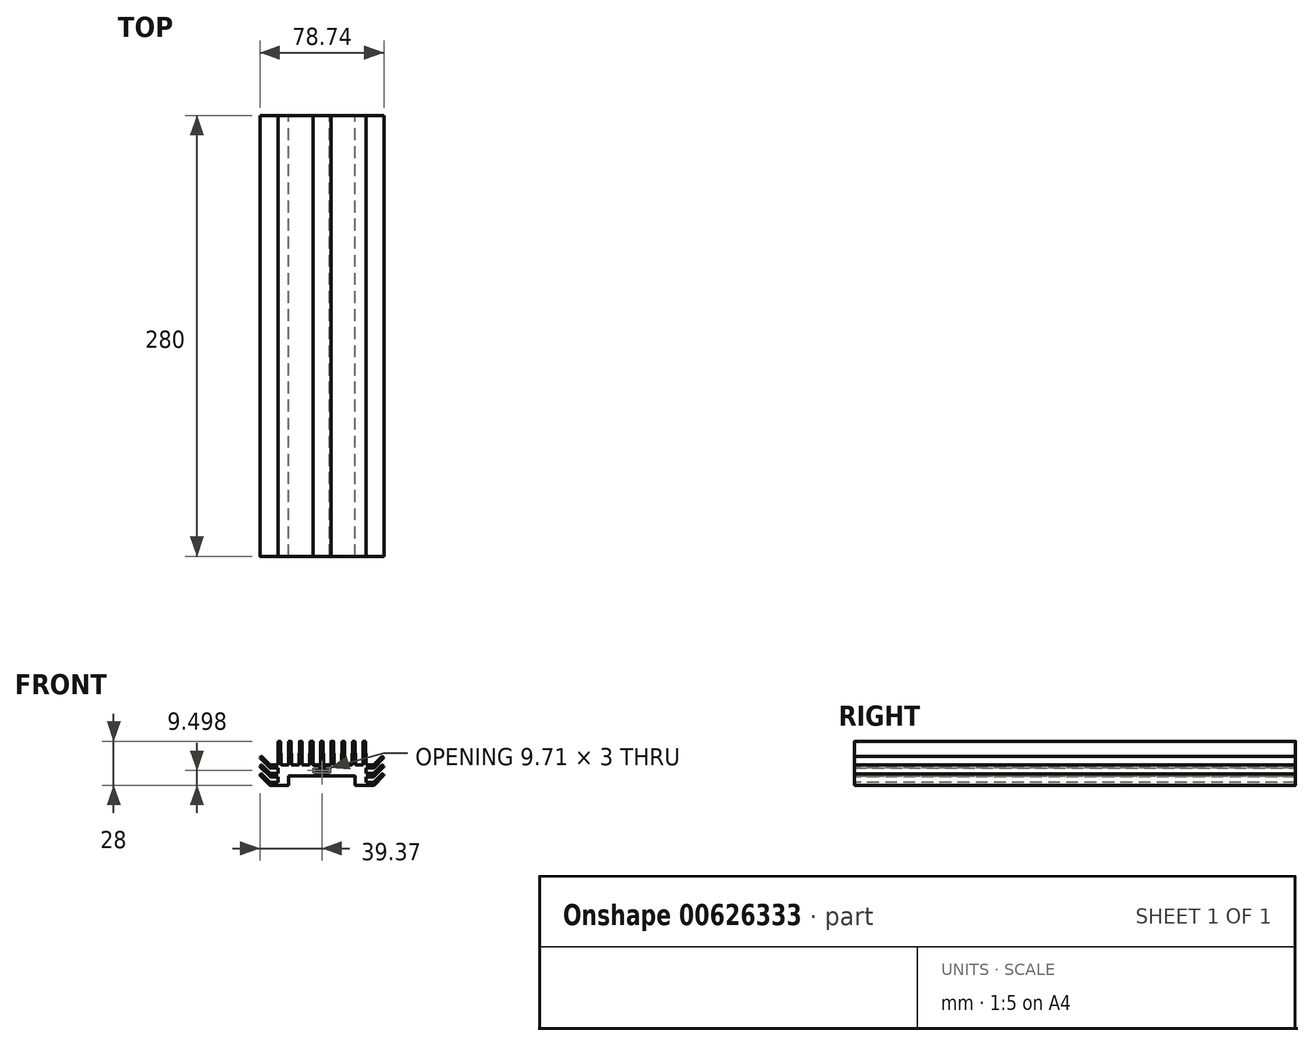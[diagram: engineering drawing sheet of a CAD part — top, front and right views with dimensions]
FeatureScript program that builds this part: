
annotation { "Feature Type Name" : "Feature", "Feature Type Description" : "" }
export const myFeature = defineFeature(function(context is Context, id is Id, definition is map)
    precondition{}
    {
        {
            var Q0;
            Q0=qCreatedBy(makeId("Front.planeOp"),FACE);
            var sketch = newSketch(context, id + "F0", { "sketchPlane" : qUnion([Q0])});
            skLineSegment(sketch, "E0.2.0.0", {"start": v(-26.25, 18.3) * mm, "end": v(-26, 3.7) * mm});
            skLineSegment(sketch, "E0.2.0.1", {"start": v(-25.8, 3.5) * mm, "end": v(-21.45, 3.5) * mm});
            skLineSegment(sketch, "E0.2.0.2", {"start": v(-28, 3.7) * mm, "end": v(-27.75, 18.3) * mm});
            skLineSegment(sketch, "E0.2.0.3", {"start": v(-27.55, 18.5) * mm, "end": v(-26.45, 18.5) * mm});
            skLineSegment(sketch, "E0.3.0.0", {"start": v(-19.5, 18.3) * mm, "end": v(-19.25, 3.7) * mm});
            skLineSegment(sketch, "E0.3.0.1", {"start": v(-19.05, 3.5) * mm, "end": v(-14.7, 3.5) * mm});
            skLineSegment(sketch, "E0.3.0.2", {"start": v(-21.25, 3.7) * mm, "end": v(-21, 18.3) * mm});
            skLineSegment(sketch, "E0.3.0.3", {"start": v(-20.8, 18.5) * mm, "end": v(-19.7, 18.5) * mm});
            skLineSegment(sketch, "E0.4.0.0", {"start": v(-12.75, 18.3) * mm, "end": v(-12.5, 3.7) * mm});
            skLineSegment(sketch, "E0.4.0.1", {"start": v(-12.3, 3.5) * mm, "end": v(-7.95, 3.5) * mm});
            skLineSegment(sketch, "E0.4.0.2", {"start": v(-14.5, 3.7) * mm, "end": v(-14.25, 18.3) * mm});
            skLineSegment(sketch, "E0.4.0.3", {"start": v(-14.05, 18.5) * mm, "end": v(-12.95, 18.5) * mm});
            skLineSegment(sketch, "E0.5.0.0", {"start": v(-5.75, 18.3) * mm, "end": v(-5.75, 3.7) * mm});
            skLineSegment(sketch, "E0.5.0.1", {"start": v(-5.55, 3.5) * mm, "end": v(-1.2, 3.5) * mm});
            skLineSegment(sketch, "E0.5.0.2", {"start": v(-7.75, 3.7) * mm, "end": v(-7.5, 18.3) * mm});
            skLineSegment(sketch, "E0.5.0.3", {"start": v(-7.3, 18.5) * mm, "end": v(-5.95, 18.5) * mm});
            skLineSegment(sketch, "E1.6.6.0", {"start": v(-1, 3.7) * mm, "end": v(-0.75, 18.3) * mm});
            skLineSegment(sketch, "E1.9.6.0", {"start": v(-0.55, 18.5) * mm, "end": v(0, 18.5) * mm});
            skPoint(sketch, "E2", {"position": v(0, 18.5) * mm});
            skLineSegment(sketch, "E3", {"start": v(0, 18.5) * mm, "end": v(0, 1.5) * mm});
            skLineSegment(sketch, "E4", {"start": v(-4.85, 1.3) * mm, "end": v(-4.85, -1.3) * mm});
            skLineSegment(sketch, "E5", {"start": v(0, -1.5) * mm, "end": v(0, -3.5) * mm});
            skPoint(sketch, "E6.visualSharp", {"position": v(-27.75, 18.5) * mm});
            skArc(sketch, "E6.filletArc", {"start": v(-27.55, 18.5) * mm, "mid": v(-27.7, 18.44) * mm, "end": v(-27.75, 18.3) * mm});
            skPoint(sketch, "E7.visualSharp", {"position": v(-26.25, 18.5) * mm});
            skArc(sketch, "E7.filletArc", {"start": v(-26.25, 18.3) * mm, "mid": v(-26.3, 18.44) * mm, "end": v(-26.45, 18.5) * mm});
            skPoint(sketch, "E8.visualSharp", {"position": v(-21, 18.5) * mm});
            skArc(sketch, "E8.filletArc", {"start": v(-20.8, 18.5) * mm, "mid": v(-20.94, 18.44) * mm, "end": v(-21, 18.3) * mm});
            skPoint(sketch, "E9.visualSharp", {"position": v(-19.5, 18.5) * mm});
            skArc(sketch, "E9.filletArc", {"start": v(-19.5, 18.3) * mm, "mid": v(-19.56, 18.44) * mm, "end": v(-19.7, 18.5) * mm});
            skPoint(sketch, "E10.visualSharp", {"position": v(-14.25, 18.5) * mm});
            skArc(sketch, "E10.filletArc", {"start": v(-14.05, 18.5) * mm, "mid": v(-14.2, 18.44) * mm, "end": v(-14.25, 18.3) * mm});
            skPoint(sketch, "E11.visualSharp", {"position": v(-12.75, 18.5) * mm});
            skArc(sketch, "E11.filletArc", {"start": v(-12.75, 18.3) * mm, "mid": v(-12.8, 18.44) * mm, "end": v(-12.95, 18.5) * mm});
            skPoint(sketch, "E12.visualSharp", {"position": v(-7.5, 18.5) * mm});
            skArc(sketch, "E12.filletArc", {"start": v(-7.3, 18.5) * mm, "mid": v(-7.44, 18.44) * mm, "end": v(-7.5, 18.3) * mm});
            skPoint(sketch, "E13.visualSharp", {"position": v(-5.75, 18.5) * mm});
            skArc(sketch, "E13.filletArc", {"start": v(-5.75, 18.3) * mm, "mid": v(-5.8, 18.44) * mm, "end": v(-5.95, 18.5) * mm});
            skPoint(sketch, "E14.visualSharp", {"position": v(-0.75, 18.5) * mm});
            skArc(sketch, "E14.filletArc", {"start": v(-0.55, 18.5) * mm, "mid": v(-0.7, 18.44) * mm, "end": v(-0.75, 18.3) * mm});
            skPoint(sketch, "E15.visualSharp", {"position": v(0, 1.5) * mm});
            skPoint(sketch, "E16.visualSharp", {"position": v(-4.85, 1.5) * mm});
            skArc(sketch, "E16.filletArc", {"start": v(-4.65, 1.5) * mm, "mid": v(-4.8, 1.44) * mm, "end": v(-4.85, 1.3) * mm});
            skPoint(sketch, "E17.visualSharp", {"position": v(-4.85, -1.5) * mm});
            skArc(sketch, "E17.filletArc", {"start": v(-4.85, -1.3) * mm, "mid": v(-4.8, -1.44) * mm, "end": v(-4.65, -1.5) * mm});
            skPoint(sketch, "E18.visualSharp", {"position": v(0, -1.5) * mm});
            skPoint(sketch, "E19.visualSharp", {"position": v(0, -3.5) * mm});
            skPoint(sketch, "E20.visualSharp", {"position": v(-26, 3.5) * mm});
            skArc(sketch, "E20.filletArc", {"start": v(-26, 3.7) * mm, "mid": v(-25.94, 3.56) * mm, "end": v(-25.8, 3.5) * mm});
            skPoint(sketch, "E21.visualSharp", {"position": v(-21.25, 3.5) * mm});
            skArc(sketch, "E21.filletArc", {"start": v(-21.45, 3.5) * mm, "mid": v(-21.3, 3.56) * mm, "end": v(-21.25, 3.7) * mm});
            skPoint(sketch, "E22.visualSharp", {"position": v(-19.25, 3.5) * mm});
            skArc(sketch, "E22.filletArc", {"start": v(-19.25, 3.7) * mm, "mid": v(-19.2, 3.56) * mm, "end": v(-19.05, 3.5) * mm});
            skPoint(sketch, "E23.visualSharp", {"position": v(-14.5, 3.5) * mm});
            skArc(sketch, "E23.filletArc", {"start": v(-14.7, 3.5) * mm, "mid": v(-14.56, 3.56) * mm, "end": v(-14.5, 3.7) * mm});
            skPoint(sketch, "E24.visualSharp", {"position": v(-12.5, 3.5) * mm});
            skArc(sketch, "E24.filletArc", {"start": v(-12.5, 3.7) * mm, "mid": v(-12.44, 3.56) * mm, "end": v(-12.3, 3.5) * mm});
            skPoint(sketch, "E25.visualSharp", {"position": v(-7.75, 3.5) * mm});
            skArc(sketch, "E25.filletArc", {"start": v(-7.95, 3.5) * mm, "mid": v(-7.8, 3.56) * mm, "end": v(-7.75, 3.7) * mm});
            skPoint(sketch, "E26.visualSharp", {"position": v(-5.75, 3.5) * mm});
            skArc(sketch, "E26.filletArc", {"start": v(-5.75, 3.7) * mm, "mid": v(-5.7, 3.56) * mm, "end": v(-5.55, 3.5) * mm});
            skPoint(sketch, "E27.visualSharp", {"position": v(-1, 3.5) * mm});
            skArc(sketch, "E27.filletArc", {"start": v(-1.2, 3.5) * mm, "mid": v(-1.06, 3.56) * mm, "end": v(-1, 3.7) * mm});
            skLineSegment(sketch, "E28", {"start": v(-4.65, 1.5) * mm, "end": v(0, 1.5) * mm});
            skLineSegment(sketch, "E29", {"start": v(-4.65, -1.5) * mm, "end": v(0, -1.5) * mm});
            skLineSegment(sketch, "E30", {"start": v(-21.15, -3.7) * mm, "end": v(-21.15, -9.3) * mm});
            skPoint(sketch, "E31.visualSharp", {"position": v(-21.15, -9.5) * mm});
            skArc(sketch, "E31.filletArc", {"start": v(-21.35, -9.5) * mm, "mid": v(-21.2, -9.44) * mm, "end": v(-21.15, -9.3) * mm});
            skPoint(sketch, "E32.visualSharp", {"position": v(-21.15, -3.5) * mm});
            skArc(sketch, "E32.filletArc", {"start": v(-20.95, -3.5) * mm, "mid": v(-21.1, -3.56) * mm, "end": v(-21.15, -3.7) * mm});
            skLineSegment(sketch, "E33", {"start": v(-28, 3.7) * mm, "end": v(-28, -9.5) * mm});
            skLineSegment(sketch, "E34", {"start": v(-21.35, -9.5) * mm, "end": v(-28, -9.5) * mm});
            skLineSegment(sketch, "E35", {"start": v(-20.95, -3.5) * mm, "end": v(0, -3.5) * mm});
            skSolve(sketch);
        }
        {
            var Q0;
            Q0=qSketchRegion(id+"F0",true);
            extrude(context, id + "F1", {"entities" : qUnion([Q0]), "depth" : 280 * mm, "offsetDistance" : 25 * mm});
        }
        {
            var Q0;
            Q0=makeQuery(id+"F1.opExtrude","CAP_FACE",FACE,{"disambiguationData":[OSD([sQuery(id+"F0.wireOp",EDGE,"bL3qZI64-7qrA-8tBo-xELN-WwCQw7n5xeQu"),sQuery(id+"F0.wireOp",EDGE,"nefEkcPL-9hmu-xnLm-Q7lG-tzpoaju1hbQN"),sQuery(id+"F0.wireOp",EDGE,"E0.1.0.0"),sQuery(id+"F0.wireOp",EDGE,"E0.1.0.1"),sQuery(id+"F0.wireOp",EDGE,"E0.1.0.2"),sQuery(id+"F0.wireOp",EDGE,"E0.1.0.3"),sQuery(id+"F0.wireOp",EDGE,"E0.2.0.0"),sQuery(id+"F0.wireOp",EDGE,"E0.2.0.1"),sQuery(id+"F0.wireOp",EDGE,"E0.2.0.2"),sQuery(id+"F0.wireOp",EDGE,"E0.2.0.3"),sQuery(id+"F0.wireOp",EDGE,"E0.3.0.0"),sQuery(id+"F0.wireOp",EDGE,"E0.3.0.1"),sQuery(id+"F0.wireOp",EDGE,"E0.3.0.2"),sQuery(id+"F0.wireOp",EDGE,"E0.3.0.3"),sQuery(id+"F0.wireOp",EDGE,"E0.4.0.0"),sQuery(id+"F0.wireOp",EDGE,"E0.4.0.1"),sQuery(id+"F0.wireOp",EDGE,"E0.4.0.2"),sQuery(id+"F0.wireOp",EDGE,"E0.4.0.3"),sQuery(id+"F0.wireOp",EDGE,"E0.5.0.0"),sQuery(id+"F0.wireOp",EDGE,"E0.5.0.1"),sQuery(id+"F0.wireOp",EDGE,"E0.5.0.2"),sQuery(id+"F0.wireOp",EDGE,"E0.5.0.3"),sQuery(id+"F0.wireOp",EDGE,"E1.6.6.0"),sQuery(id+"F0.wireOp",EDGE,"E1.9.6.0"),sQuery(id+"F0.wireOp",EDGE,"E3"),sQuery(id+"F0.wireOp",EDGE,"E4"),sQuery(id+"F0.wireOp",EDGE,"E5"),sQuery(id+"F0.wireOp",EDGE,"mlO0Lyb2-eVYo-AatF-SlvP-83DAQH0pbuAu"),sQuery(id+"F0.wireOp",EDGE,"1c295024-f0d5-4380-9586-7d7894610ec9.filletArc"),sQuery(id+"F0.wireOp",EDGE,"2c5bb03b-c66e-477a-8ee8-765ec2279287.filletArc"),sQuery(id+"F0.wireOp",EDGE,"E6.filletArc"),sQuery(id+"F0.wireOp",EDGE,"E7.filletArc"),sQuery(id+"F0.wireOp",EDGE,"E8.filletArc"),sQuery(id+"F0.wireOp",EDGE,"E9.filletArc"),sQuery(id+"F0.wireOp",EDGE,"E10.filletArc"),sQuery(id+"F0.wireOp",EDGE,"E11.filletArc"),sQuery(id+"F0.wireOp",EDGE,"E12.filletArc"),sQuery(id+"F0.wireOp",EDGE,"E13.filletArc"),sQuery(id+"F0.wireOp",EDGE,"E14.filletArc"),sQuery(id+"F0.wireOp",EDGE,"E16.filletArc"),sQuery(id+"F0.wireOp",EDGE,"E17.filletArc"),sQuery(id+"F0.wireOp",EDGE,"3fa5c7a0-46de-4f7c-b7f0-d3e079dab4d4.filletArc"),sQuery(id+"F0.wireOp",EDGE,"1a05ea91-b8e8-4e60-8976-cabcb86d6e5d.filletArc"),sQuery(id+"F0.wireOp",EDGE,"4ed3edbc-86c1-4c2d-b3db-7962da8c7f3b.filletArc"),sQuery(id+"F0.wireOp",EDGE,"df53fec7-61cd-4923-a6ae-b9e3b851a0f2.filletArc"),sQuery(id+"F0.wireOp",EDGE,"27feb3de-e673-4ea3-928d-deec6766394d.filletArc"),sQuery(id+"F0.wireOp",EDGE,"473c6a5f-9318-4648-8a10-d55a2b371333.filletArc"),sQuery(id+"F0.wireOp",EDGE,"E20.filletArc"),sQuery(id+"F0.wireOp",EDGE,"E21.filletArc"),sQuery(id+"F0.wireOp",EDGE,"E22.filletArc"),sQuery(id+"F0.wireOp",EDGE,"E23.filletArc"),sQuery(id+"F0.wireOp",EDGE,"E24.filletArc"),sQuery(id+"F0.wireOp",EDGE,"E25.filletArc"),sQuery(id+"F0.wireOp",EDGE,"E26.filletArc"),sQuery(id+"F0.wireOp",EDGE,"E27.filletArc"),sQuery(id+"F0.wireOp",EDGE,"E28"),sQuery(id+"F0.wireOp",EDGE,"E29"),sQuery(id+"F0.wireOp",EDGE,"uo7RkyCL-c98j-zEhM-1sWP-hJWaIm8JIuHS"),sQuery(id+"F0.wireOp",EDGE,"UyrvhKvo-Hriy-DGAL-Pid4-MuuIVOQ2I04g"),sQuery(id+"F0.wireOp",EDGE,"U6ICKPt3-iNcd-rmJ2-pTeO-fHKRQgZmkzro"),sQuery(id+"F0.wireOp",EDGE,"cJHcNlIk-0kYQ-5AfO-mOoR-XwhJbZEzOTLT"),sQuery(id+"F0.wireOp",EDGE,"E30"),sQuery(id+"F0.wireOp",EDGE,"E31.filletArc"),sQuery(id+"F0.wireOp",EDGE,"1ba531c4-4689-4158-b5fc-088271326b5e.filletArc"),sQuery(id+"F0.wireOp",EDGE,"E32.filletArc")])],"isStart":false});
            var sketch = newSketch(context, id + "F2", { "sketchPlane" : qUnion([Q0])});
            skLineSegment(sketch, "E36", {"start": v(-28, -7.5) * mm, "end": v(-32.79, -7.5) * mm});
            skLineSegment(sketch, "E37", {"start": v(-28, -9.5) * mm, "end": v(-33, -9.5) * mm});
            skLineSegment(sketch, "E38", {"start": v(-32.93, -7.45) * mm, "end": v(-38.25, -2.13) * mm});
            skLineSegment(sketch, "E39", {"start": v(-33.06, -9.44) * mm, "end": v(-39.3, -3.19) * mm});
            skLineSegment(sketch, "E40", {"start": v(-38.53, -2.13) * mm, "end": v(-39.3, -2.9) * mm});
            skLineSegment(sketch, "E41", {"start": v(-28, -7.5) * mm, "end": v(-28, -9.5) * mm});
            skLineSegment(sketch, "E42.direction2", {"start": v(-33, -9.5) * mm, "end": v(-33, -4) * mm, "construction": true});
            skPoint(sketch, "E43.visualSharp", {"position": v(-32.87, -7.5) * mm});
            skArc(sketch, "E43.filletArc", {"start": v(-32.93, -7.45) * mm, "mid": v(-32.87, -7.49) * mm, "end": v(-32.79, -7.5) * mm});
            skPoint(sketch, "E44.visualSharp", {"position": v(-38.39, -1.99) * mm});
            skArc(sketch, "E44.filletArc", {"start": v(-38.25, -2.13) * mm, "mid": v(-38.39, -2.07) * mm, "end": v(-38.53, -2.13) * mm});
            skPoint(sketch, "E45.visualSharp", {"position": v(-39.45, -3.05) * mm});
            skArc(sketch, "E45.filletArc", {"start": v(-39.3, -2.9) * mm, "mid": v(-39.37, -3.05) * mm, "end": v(-39.3, -3.19) * mm});
            skPoint(sketch, "E46.visualSharp", {"position": v(-33, -9.5) * mm});
            skArc(sketch, "E46.filletArc", {"start": v(-33.06, -9.44) * mm, "mid": v(-33, -9.48) * mm, "end": v(-32.91, -9.5) * mm});
            skLineSegment(sketch, "E47.0.1.0", {"start": v(-32.93, -1.95) * mm, "end": v(-38.25, 3.37) * mm});
            skLineSegment(sketch, "E47.0.1.1", {"start": v(-33.06, -3.94) * mm, "end": v(-39.3, 2.31) * mm});
            skPoint(sketch, "E47.0.1.2", {"position": v(-38.39, 3.51) * mm});
            skLineSegment(sketch, "E47.0.1.3", {"start": v(-28, -4) * mm, "end": v(-33, -4) * mm});
            skLineSegment(sketch, "E47.0.1.4", {"start": v(-28, -2) * mm, "end": v(-28, -4) * mm});
            skPoint(sketch, "E47.0.1.5", {"position": v(-33, -4) * mm});
            skLineSegment(sketch, "E47.0.1.6", {"start": v(-28, -2) * mm, "end": v(-32.79, -2) * mm});
            skPoint(sketch, "E47.0.1.7", {"position": v(-39.45, 2.45) * mm});
            skPoint(sketch, "E47.0.1.8", {"position": v(-32.87, -2) * mm});
            skLineSegment(sketch, "E47.0.1.9", {"start": v(-33, -4) * mm, "end": v(-33, 1.5) * mm, "construction": true});
            skLineSegment(sketch, "E47.0.1.10", {"start": v(-33, -4) * mm, "end": v(-33, 1.5) * mm, "construction": true});
            skLineSegment(sketch, "E47.0.1.11", {"start": v(-38.53, 3.37) * mm, "end": v(-39.3, 2.6) * mm});
            skArc(sketch, "E47.0.1.12", {"start": v(-38.25, 3.37) * mm, "mid": v(-38.39, 3.43) * mm, "end": v(-38.53, 3.37) * mm});
            skArc(sketch, "E47.0.1.13", {"start": v(-39.3, 2.6) * mm, "mid": v(-39.37, 2.45) * mm, "end": v(-39.3, 2.31) * mm});
            skArc(sketch, "E47.0.1.14", {"start": v(-32.93, -1.95) * mm, "mid": v(-32.87, -1.99) * mm, "end": v(-32.79, -2) * mm});
            skArc(sketch, "E47.0.1.15", {"start": v(-33.06, -3.94) * mm, "mid": v(-33, -3.98) * mm, "end": v(-32.91, -4) * mm});
            skLineSegment(sketch, "E47.0.2.0", {"start": v(-32.93, 3.55) * mm, "end": v(-38.25, 8.87) * mm});
            skLineSegment(sketch, "E47.0.2.1", {"start": v(-33.06, 1.56) * mm, "end": v(-39.3, 7.81) * mm});
            skPoint(sketch, "E47.0.2.2", {"position": v(-38.39, 9.01) * mm});
            skLineSegment(sketch, "E47.0.2.3", {"start": v(-28, 1.5) * mm, "end": v(-33, 1.5) * mm});
            skLineSegment(sketch, "E47.0.2.4", {"start": v(-28, 3.5) * mm, "end": v(-28, 1.5) * mm});
            skPoint(sketch, "E47.0.2.5", {"position": v(-33, 1.5) * mm});
            skLineSegment(sketch, "E47.0.2.6", {"start": v(-28, 3.5) * mm, "end": v(-32.79, 3.5) * mm});
            skPoint(sketch, "E47.0.2.7", {"position": v(-39.45, 7.95) * mm});
            skPoint(sketch, "E47.0.2.8", {"position": v(-32.87, 3.5) * mm});
            skLineSegment(sketch, "E47.0.2.9", {"start": v(-33, 1.5) * mm, "end": v(-33, 7) * mm, "construction": true});
            skLineSegment(sketch, "E47.0.2.10", {"start": v(-33, 1.5) * mm, "end": v(-33, 7) * mm, "construction": true});
            skLineSegment(sketch, "E47.0.2.11", {"start": v(-38.53, 8.87) * mm, "end": v(-39.3, 8.1) * mm});
            skArc(sketch, "E47.0.2.12", {"start": v(-38.25, 8.87) * mm, "mid": v(-38.39, 8.93) * mm, "end": v(-38.53, 8.87) * mm});
            skArc(sketch, "E47.0.2.13", {"start": v(-39.3, 8.1) * mm, "mid": v(-39.37, 7.95) * mm, "end": v(-39.3, 7.81) * mm});
            skArc(sketch, "E47.0.2.14", {"start": v(-32.93, 3.55) * mm, "mid": v(-32.87, 3.51) * mm, "end": v(-32.79, 3.5) * mm});
            skArc(sketch, "E47.0.2.15", {"start": v(-33.06, 1.56) * mm, "mid": v(-33, 1.52) * mm, "end": v(-32.91, 1.5) * mm});
            skLineSegment(sketch, "E47.direction1", {"start": v(-33, -9.5) * mm, "end": v(-8, -9.5) * mm, "construction": true});
            skSolve(sketch);
        }
        {
            var Q0;
            Q0=qSketchRegion(id+"F2",true);
            extrude(context, id + "F3", {"entities" : qUnion([Q0]), "operationType" : NewBodyOperationType.ADD, "oppositeDirection" : true, "depth" : 280 * mm, "offsetDistance" : 25 * mm});
        }
        {
            var Q0;
            Q0=makeQuery(id+"F1.opExtrude","SWEPT_BODY",BODY,{"disambiguationData":[OSD([sQuery(id+"F0.wireOp",EDGE,"QOM90pkH-KK3E-2t4G-PR0d-VXwYNY4fjtTb"),sQuery(id+"F0.wireOp",EDGE,"Wt8m1K6G-Pg8W-yz88-BKp3-o8GU5yjb4NPO"),sQuery(id+"F0.wireOp",EDGE,"F3vcOgBq-LlWr-xvjw-e04Y-niSAJOFfG4p2"),sQuery(id+"F0.wireOp",EDGE,"u1mY0JJN-f7Kk-nBfH-W6HL-n9qIg2MDpbPP"),sQuery(id+"F0.wireOp",EDGE,"QIDlm4V3-j7gJ-oFi3-cvUC-kSezUPiWFmIS"),sQuery(id+"F0.wireOp",EDGE,"6xrvO9A8-pm1h-AeFb-QTYX-2HOc3FF3rfEQ"),sQuery(id+"F0.wireOp",EDGE,"Nf9yDHwn-gt6s-M4IA-LLNt-3061gzFxuUBp"),sQuery(id+"F0.wireOp",EDGE,"WuwbFeWC-LNyf-1R1Z-RHmS-f9KyMF8TMt9i"),sQuery(id+"F0.wireOp",EDGE,"UM4JaTJU-Vk1M-XgEN-ImDx-eCgJd49Y6FMu"),sQuery(id+"F0.wireOp",EDGE,"OvlMNyBG-IFKC-w7DX-ZWVS-3YzXS4CVPNQT"),sQuery(id+"F0.wireOp",EDGE,"jmIuwl2N-ih4h-DjTB-hYCO-kHODNnBOpXJs"),sQuery(id+"F0.wireOp",EDGE,"bhDqv4Mq-hX6j-4xH4-fuLw-w89xF4HoMTrF"),sQuery(id+"F0.wireOp",EDGE,"bL3qZI64-7qrA-8tBo-xELN-WwCQw7n5xeQu"),sQuery(id+"F0.wireOp",EDGE,"nefEkcPL-9hmu-xnLm-Q7lG-tzpoaju1hbQN"),sQuery(id+"F0.wireOp",EDGE,"DATJw4Rr-6OHI-e9sL-mig8-pdpoUj6XXJZJ"),sQuery(id+"F0.wireOp",EDGE,"ed90f767-a289-48e3-8617-8c3c22fb4d72.trimOffspring"),sQuery(id+"F0.wireOp",EDGE,"7ho3JKrC-G9q0-DxLB-qz2V-eUSqsKLsZmBJ"),sQuery(id+"F0.wireOp",EDGE,"Nb5lTvUm-lXxh-YIyg-5x1b-LZ3tmgTk2abY"),sQuery(id+"F0.wireOp",EDGE,"Z2SCv61l-lqp3-au7K-zo4L-WJUViGbaLhYw"),sQuery(id+"F0.wireOp",EDGE,"qlelKb4N-GS20-CHXp-tJnn-sWviO8Gk2iGX"),sQuery(id+"F0.wireOp",EDGE,"E0.1.0.0"),sQuery(id+"F0.wireOp",EDGE,"E0.1.0.1"),sQuery(id+"F0.wireOp",EDGE,"E0.1.0.2"),sQuery(id+"F0.wireOp",EDGE,"E0.1.0.3"),sQuery(id+"F0.wireOp",EDGE,"E0.2.0.0"),sQuery(id+"F0.wireOp",EDGE,"E0.2.0.1"),sQuery(id+"F0.wireOp",EDGE,"E0.2.0.2"),sQuery(id+"F0.wireOp",EDGE,"E0.2.0.3"),sQuery(id+"F0.wireOp",EDGE,"E0.3.0.0"),sQuery(id+"F0.wireOp",EDGE,"E0.3.0.1"),sQuery(id+"F0.wireOp",EDGE,"E0.3.0.2"),sQuery(id+"F0.wireOp",EDGE,"E0.3.0.3"),sQuery(id+"F0.wireOp",EDGE,"E0.4.0.0"),sQuery(id+"F0.wireOp",EDGE,"E0.4.0.1"),sQuery(id+"F0.wireOp",EDGE,"E0.4.0.2"),sQuery(id+"F0.wireOp",EDGE,"E0.4.0.3"),sQuery(id+"F0.wireOp",EDGE,"E0.5.0.0"),sQuery(id+"F0.wireOp",EDGE,"E0.5.0.1"),sQuery(id+"F0.wireOp",EDGE,"E0.5.0.2"),sQuery(id+"F0.wireOp",EDGE,"E0.5.0.3"),sQuery(id+"F0.wireOp",EDGE,"E1.6.6.0"),sQuery(id+"F0.wireOp",EDGE,"E1.9.6.0"),sQuery(id+"F0.wireOp",EDGE,"yGFb3Jfo-Lhlh-xzfz-Ljs9-34xcXF1H7Gp1"),sQuery(id+"F0.wireOp",EDGE,"dxc8wIRG-n3ac-7oqY-UQSt-FR4flQWY79jH"),sQuery(id+"F0.wireOp",EDGE,"pMfyub31-Xo22-kmQh-hgcO-EaUa3d53Z9ym"),sQuery(id+"F0.wireOp",EDGE,"EXS0VTzR-uZRH-gpkk-ciJv-APifiNII5ex7"),sQuery(id+"F0.wireOp",EDGE,"j9COY3aO-4lFf-zBAU-mgS4-eOpnypJtWWPn")])]});
            var Q1;
            Q1=makeQuery(id+"F1.opExtrude","SWEPT_FACE",FACE,{"disambiguationData":[OSD([sQuery(id+"F0.wireOp",EDGE,"E3")])]});
            mirror(context, id + "F4", {"operationType" : NewBodyOperationType.ADD, "entities" : qUnion([Q0]), "mirrorPlane" : qUnion([Q1])});
        }
    });
